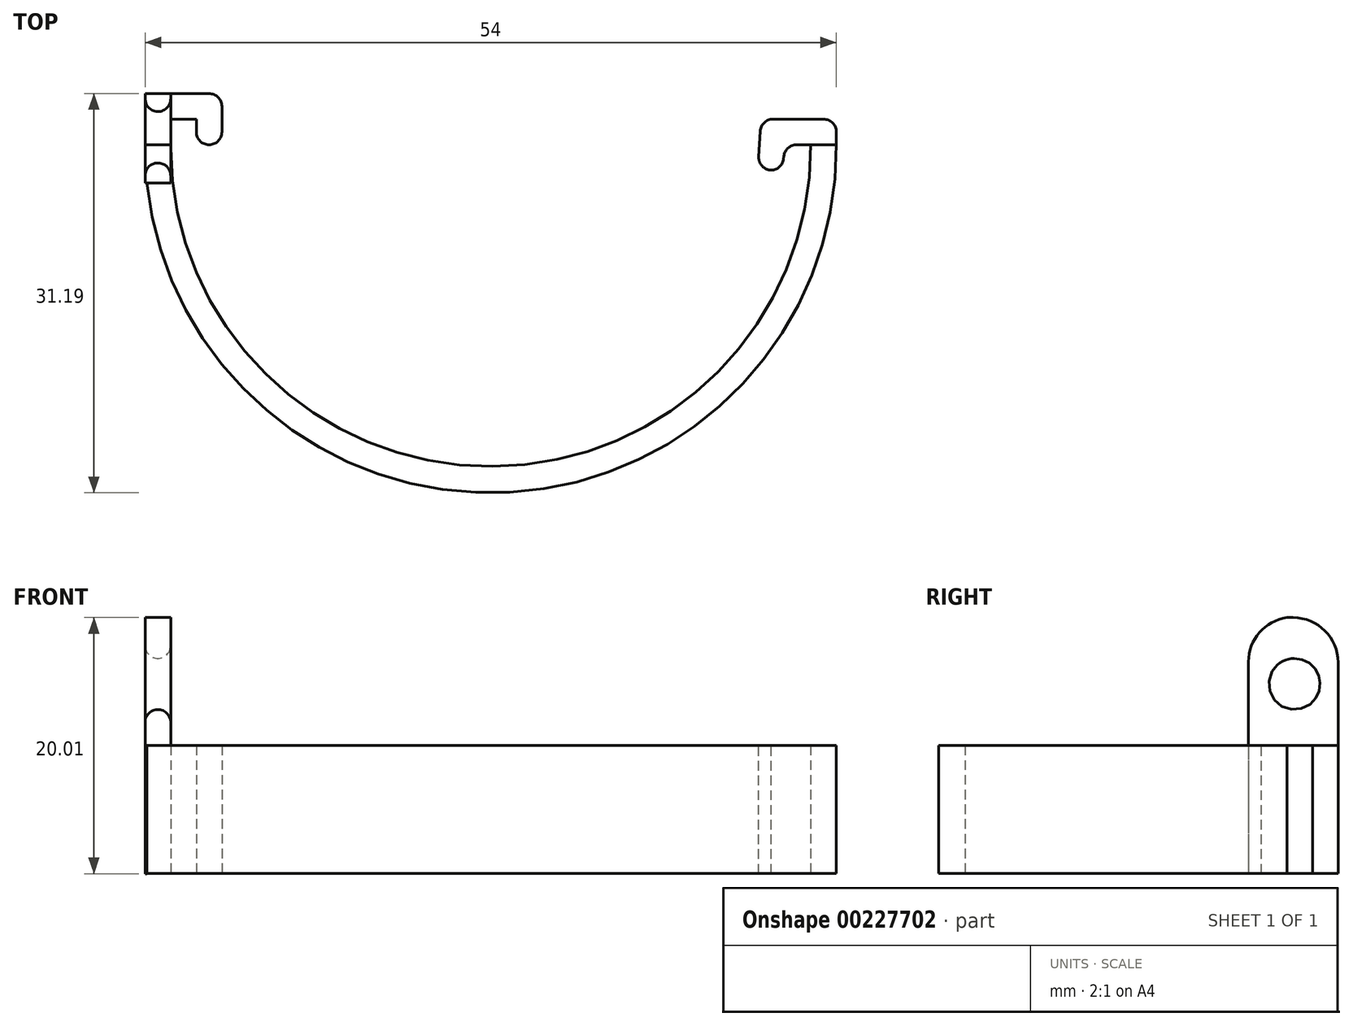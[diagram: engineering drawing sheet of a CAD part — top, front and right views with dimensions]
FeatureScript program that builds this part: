
annotation { "Feature Type Name" : "Feature", "Feature Type Description" : "" }
export const myFeature = defineFeature(function(context is Context, id is Id, definition is map)
    precondition{}
    {
        {
            var Q0;
            Q0=qCreatedBy(makeId("Top.planeOp"),FACE);
            var sketch = newSketch(context, id + "F0", { "sketchPlane" : qUnion([Q0])});
            skArc(sketch, "E0", {"start": v(-64.73, 0) * mm, "mid": v(-39.73, -25.13) * mm, "end": v(-14.73, 0) * mm});
            skLineSegment(sketch, "E1", {"start": v(-64.73, 0) * mm, "end": v(-66.73, 0) * mm});
            skLineSegment(sketch, "E2", {"start": v(-14.73, 0) * mm, "end": v(-12.73, 0) * mm});
            skArc(sketch, "E3", {"start": v(-66.73, 0) * mm, "mid": v(-39.73, -27.19) * mm, "end": v(-12.73, 0) * mm});
            skLineSegment(sketch, "E4", {"start": v(-64.73, 0) * mm, "end": v(-64.73, 2) * mm});
            skLineSegment(sketch, "E5", {"start": v(-64.73, 2) * mm, "end": v(-62.73, 2) * mm});
            skLineSegment(sketch, "E6", {"start": v(-62.73, 2) * mm, "end": v(-62.73, 0) * mm});
            skLineSegment(sketch, "E7", {"start": v(-62.73, 0) * mm, "end": v(-60.73, 0) * mm});
            skLineSegment(sketch, "E8", {"start": v(-60.73, 0) * mm, "end": v(-60.73, 4) * mm});
            skLineSegment(sketch, "E9", {"start": v(-60.73, 4) * mm, "end": v(-66.73, 4) * mm});
            skLineSegment(sketch, "E10", {"start": v(-66.73, 4) * mm, "end": v(-66.73, 0) * mm});
            skSolve(sketch);
        }
        {
            var Q0;
            Q0=makeQuery(id+"F0.imprint","IMPRINT",FACE,{"disambiguationData":[TD([[makeQuery(id+"F0.imprint","IMPRINT",EDGE,{"derivedFrom":sQuery(id+"F0.wireOp",EDGE,"E0")}),-1.0]])]});
            var sketch = newSketch(context, id + "F1", { "sketchPlane" : qUnion([Q0])});
            skLineSegment(sketch, "E11", {"start": v(-14.74, 0) * mm, "end": v(-18.74, 0) * mm});
            skLineSegment(sketch, "E12", {"start": v(-18.74, 0) * mm, "end": v(-18.74, -4) * mm});
            skLineSegment(sketch, "E13", {"start": v(-18.74, -4) * mm, "end": v(-17.14, -4) * mm});
            skLineSegment(sketch, "E14", {"start": v(-16.74, -2) * mm, "end": v(-14.74, -2) * mm});
            skLineSegment(sketch, "E15", {"start": v(-14.74, -2) * mm, "end": v(-14.74, 0) * mm});
            skLineSegment(sketch, "E16", {"start": v(-17.14, -4) * mm, "end": v(-16.74, -2) * mm});
            skSolve(sketch);
        }
        {
            var Q0;
            {var subQ0=makeQuery(id+"F0.imprint","IMPRINT",EDGE,{"derivedFrom":sQuery(id+"F0.wireOp",EDGE,"E1")});Q0=makeQuery(id+"F1.imprint","IMPRINT",FACE,{"disambiguationData":[TD([[makeQuery(id+"F1.imprint","IMPRINT",EDGE,{"derivedFrom":subQ0}),1.0]])]});}
            var Q1;
            Q1 = qSketchRegion(id + "F0", true);
            extrude(context, id + "F2", {"entities" : qUnion([Q0, Q1]), "depth" : 10 * mm});
        }
        {
            var Q0;
            Q0=makeQuery(id+"F2.opExtrude","CAP_FACE",FACE,{"disambiguationData":[OSD([sQuery(id+"F0.wireOp",EDGE,"E0"),sQuery(id+"F0.wireOp",EDGE,"E2"),sQuery(id+"F0.wireOp",EDGE,"E3"),sQuery(id+"F0.wireOp",EDGE,"E4"),sQuery(id+"F0.wireOp",EDGE,"E5"),sQuery(id+"F0.wireOp",EDGE,"E6"),sQuery(id+"F0.wireOp",EDGE,"E7"),sQuery(id+"F0.wireOp",EDGE,"E8"),sQuery(id+"F0.wireOp",EDGE,"E9"),sQuery(id+"F0.wireOp",EDGE,"E10")])],"isStart":false});
            var sketch = newSketch(context, id + "F3", { "sketchPlane" : qUnion([Q0])});
            skLineSegment(sketch, "E17.bottom", {"start": v(-64.73, 0) * mm, "end": v(-66.8, 0) * mm});
            skLineSegment(sketch, "E17.top", {"start": v(-64.73, 4) * mm, "end": v(-66.8, 4) * mm});
            skLineSegment(sketch, "E17.left", {"start": v(-64.73, 0) * mm, "end": v(-64.73, 4) * mm});
            skLineSegment(sketch, "E17.right", {"start": v(-66.8, 0) * mm, "end": v(-66.8, 4) * mm});
            skSolve(sketch);
        }
        {
            var Q0;
            {var subQ1=sQuery(id+"F0.wireOp",EDGE,"E10");var subQ15=makeQuery(id+"F2.opExtrude","CAP_EDGE",EDGE,{"disambiguationData":[OSD([subQ1])],"isStart":false});Q0=makeQuery(id+"F3.imprint","IMPRINT",FACE,{"disambiguationData":[TD([[makeQuery(id+"F3.imprint","IMPRINT",EDGE,{"derivedFrom":subQ15}),1.0]])]});}
            extrude(context, id + "F4", {"entities" : qUnion([Q0]), "operationType" : NewBodyOperationType.ADD, "depth" : 10 * mm});
        }
        {
            var Q0;
            Q0=makeQuery(id+"F4.opExtrude","SWEPT_FACE",FACE,{"disambiguationData":[OSD([sQuery(id+"F3.wireOp",EDGE,"E17.bottom")])]});
            extrude(context, id + "F5", {"entities" : qUnion([Q0]), "depth" : 3 * mm});
        }
        {
            var Q0;
            {var subQ0=sQuery(id+"F3.wireOp",EDGE,"E17.bottom");Q0=makeQuery(id+"F5.opExtrude","CAP_EDGE",EDGE,{"disambiguationData":[OSD([subQ0]),TDD([makeQuery(id+"F4.opExtrude","CAP_EDGE",EDGE,{"disambiguationData":[OSD([subQ0])],"isStart":false})])],"isStart":false});}
            var Q1;
            Q1=makeQuery(id+"F4.opExtrude","CAP_EDGE",EDGE,{"disambiguationData":[OSD([sQuery(id+"F3.wireOp",EDGE,"E17.top")])],"isStart":false});
            fillet(context, id + "F6", {"entities" : qUnion([Q0, Q1]), "radius" : 3.5 * mm, "tangentPropagation" : true, "allowEdgeOverflow" : false});
        }
        {
            var Q0;
            Q0=makeQuery(id+"F4.boolean.opBoolean","MERGE",FACE,{"derivedFrom":[makeQuery(id+"F2.opExtrude","SWEPT_FACE",FACE,{"disambiguationData":[OSD([sQuery(id+"F0.wireOp",EDGE,"E4")])]}),makeQuery(id+"F4.opExtrude","SWEPT_FACE",FACE,{"disambiguationData":[OSD([sQuery(id+"F3.wireOp",EDGE,"E17.left")])]})]});
            var sketch = newSketch(context, id + "F7", { "sketchPlane" : qUnion([Q0])});
            skCircle(sketch, "E18", {"center": v(0.6, 14.82) * mm, "radius": 2 * mm});
            skSolve(sketch);
        }
        {
            var Q0;
            {var subQ0=sQuery(id+"F7.wireOp",EDGE,"E18");var subQ1=makeQuery(id+"F4.opExtrude","SWEPT_EDGE",EDGE,{"disambiguationData":[OSD([sQuery(id+"F0.wireOp",EDGE,"E0"),sQuery(id+"F3.wireOp",EDGE,"E17.bottom"),sQuery(id+"F3.wireOp",EDGE,"E17.left")])]});var subQ2=makeQuery(id+"F7.imprint","INTERSECT",VERTEX,{"disambiguationData":[OD(0.0)],"derivedFrom":[subQ1,subQ0]});Q0=makeQuery(id+"F7.imprint","IMPRINT",FACE,{"disambiguationData":[TD([[makeQuery(id+"F7.imprint","IMPRINT",EDGE,{"disambiguationData":[TD([[subQ2,-1.0]])],"derivedFrom":subQ0}),1.0]])]});}
            extrude(context, id + "F8", {"entities" : qUnion([Q0]), "operationType" : NewBodyOperationType.REMOVE, "oppositeDirection" : true, "depth" : 25.4 * mm});
        }
        {
            var Q0;
            Q0 = qSketchRegion(id + "F7", true);
            extrude(context, id + "F9", {"entities" : qUnion([Q0]), "operationType" : NewBodyOperationType.REMOVE, "oppositeDirection" : true, "depth" : 25.4 * mm});
        }
        {
            var Q0;
            {var subQ0=sQuery(id+"F3.wireOp",EDGE,"E17.bottom");Q0=makeQuery(id+"F5.opExtrude","SWEPT_FACE",FACE,{"disambiguationData":[OSD([subQ0]),TDD([makeQuery(id+"F4.opExtrude","CAP_EDGE",EDGE,{"disambiguationData":[OSD([subQ0])],"isStart":true})])]});}
            extrude(context, id + "F10", {"entities" : qUnion([Q0]), "operationType" : NewBodyOperationType.ADD, "depth" : 10 * mm});
        }
        {
            var Q0;
            {var subQ0=sQuery(id+"F0.wireOp",EDGE,"E3");var subQ1=sQuery(id+"F0.wireOp",EDGE,"E2");var subQ2=sQuery(id+"F0.wireOp",EDGE,"E4");var subQ3=sQuery(id+"F0.wireOp",EDGE,"E0");var subQ4=sQuery(id+"F0.wireOp",EDGE,"E10");Q0=makeQuery(id+"F4.boolean.opBoolean","SPLIT",FACE,{"disambiguationData":[TD([makeQuery(id+"F2.opExtrude","SWEPT_FACE",FACE,{"disambiguationData":[OSD([subQ4])]})])],"derivedFrom":makeQuery(id+"F2.opExtrude","CAP_FACE",FACE,{"disambiguationData":[OSD([subQ3,subQ1,subQ0,subQ2,sQuery(id+"F0.wireOp",EDGE,"E5"),sQuery(id+"F0.wireOp",EDGE,"E6"),sQuery(id+"F0.wireOp",EDGE,"E7"),sQuery(id+"F0.wireOp",EDGE,"E8"),sQuery(id+"F0.wireOp",EDGE,"E9"),subQ4])],"isStart":false})});}
            var sketch = newSketch(context, id + "F11", { "sketchPlane" : qUnion([Q0])});
            skLineSegment(sketch, "E19", {"start": v(-14.73, 0) * mm, "end": v(-16.73, 0) * mm});
            skLineSegment(sketch, "E20", {"start": v(-16.73, 0) * mm, "end": v(-16.96, -1.99) * mm});
            skLineSegment(sketch, "E21", {"start": v(-16.96, -1.99) * mm, "end": v(-18.86, -1.99) * mm});
            skLineSegment(sketch, "E22", {"start": v(-18.86, -1.99) * mm, "end": v(-18.63, 2) * mm});
            skLineSegment(sketch, "E23", {"start": v(-18.63, 2) * mm, "end": v(-12.73, 2) * mm});
            skLineSegment(sketch, "E24", {"start": v(-12.73, 2) * mm, "end": v(-12.73, 0) * mm});
            skLineSegment(sketch, "E25", {"start": v(-12.73, 0) * mm, "end": v(-14.73, 0) * mm});
            skSolve(sketch);
        }
        {
            var Q0;
            Q0=makeQuery(id+"F11.imprint","IMPRINT",FACE,{"disambiguationData":[TD([[makeQuery(id+"F11.imprint","IMPRINT",EDGE,{"derivedFrom":sQuery(id+"F11.wireOp",EDGE,"E19")}),-1.0]])]});
            extrude(context, id + "F12", {"entities" : qUnion([Q0]), "oppositeDirection" : true, "depth" : 10 * mm});
        }
        {
            var Q0;
            Q0=makeQuery(id+"F12.opExtrude","SWEPT_EDGE",EDGE,{"disambiguationData":[OSD([sQuery(id+"F11.wireOp",EDGE,"E19"),sQuery(id+"F11.wireOp",EDGE,"E20")])]});
            var Q1;
            Q1=makeQuery(id+"F12.opExtrude","SWEPT_EDGE",EDGE,{"disambiguationData":[OSD([sQuery(id+"F11.wireOp",EDGE,"E20"),sQuery(id+"F11.wireOp",EDGE,"E21")])]});
            var Q2;
            Q2=makeQuery(id+"F12.opExtrude","SWEPT_EDGE",EDGE,{"disambiguationData":[OSD([sQuery(id+"F11.wireOp",EDGE,"E21"),sQuery(id+"F11.wireOp",EDGE,"E22")])]});
            var Q3;
            Q3=makeQuery(id+"F12.opExtrude","SWEPT_EDGE",EDGE,{"disambiguationData":[OSD([sQuery(id+"F11.wireOp",EDGE,"E22"),sQuery(id+"F11.wireOp",EDGE,"E23")])]});
            var Q4;
            Q4=makeQuery(id+"F12.opExtrude","SWEPT_EDGE",EDGE,{"disambiguationData":[OSD([sQuery(id+"F11.wireOp",EDGE,"E23"),sQuery(id+"F11.wireOp",EDGE,"E24")])]});
            fillet(context, id + "F13", {"entities" : qUnion([Q0, Q1, Q2, Q3, Q4]), "radius" : 1 * mm, "tangentPropagation" : true, "allowEdgeOverflow" : false});
        }
        {
            var Q0;
            Q0=makeQuery(id+"F2.opExtrude","SWEPT_EDGE",EDGE,{"disambiguationData":[OSD([sQuery(id+"F0.wireOp",EDGE,"E6"),sQuery(id+"F0.wireOp",EDGE,"E7")])]});
            var Q1;
            Q1=makeQuery(id+"F2.opExtrude","SWEPT_EDGE",EDGE,{"disambiguationData":[OSD([sQuery(id+"F0.wireOp",EDGE,"E7"),sQuery(id+"F0.wireOp",EDGE,"E8")])]});
            var Q2;
            Q2=makeQuery(id+"F2.opExtrude","SWEPT_EDGE",EDGE,{"disambiguationData":[OSD([sQuery(id+"F0.wireOp",EDGE,"E8"),sQuery(id+"F0.wireOp",EDGE,"E9")])]});
            var Q3;
            Q3=makeQuery(id+"F8.boolean.opBoolean","COPY",FACE,{"derivedFrom":makeQuery(id+"F8.opExtrude","SWEPT_FACE",FACE,{"disambiguationData":[OSD([sQuery(id+"F7.wireOp",EDGE,"E18")])]})});
            var Q4;
            Q4=makeQuery(id+"F9.boolean.opBoolean","COPY",EDGE,{"derivedFrom":makeQuery(id+"F9.opExtrude","CAP_EDGE",EDGE,{"disambiguationData":[OSD([sQuery(id+"F7.wireOp",EDGE,"E18")])],"isStart":true})});
            fillet(context, id + "F14", {"entities" : qUnion([Q0, Q1, Q2, Q3, Q4]), "radius" : 1 * mm, "tangentPropagation" : true, "allowEdgeOverflow" : false});
        }
    });
